# Revit family: Haworth_Planes_ConferenceTable_RectangularTwoPiece
name_source: partatom
category: Furniture Systems
revit_build: Autodesk Revit 2018 (Build: 20170223_1515(x64)
units: mm (PartAtom-declared; Revit-internal decimal feet)

## family parameters
Always vertical = Yes
Cut with Voids When Loaded = No
OmniClass Number = 23.40.70.14.64.21
OmniClass Title = Systems Furniture
Part Type = Normal
Room Calculation Point = No
Round Connector Dimension = Use Diameter
Shared = No
Work Plane-Based = No

## types (36) — shared parameters
Actual Height = 29"
Actual Width = 121"
Assembly Code = E2020200
Base Finish = Haworth _ Laminate _ Maple H-AE
Cable Base = Yes
Center Leg_Interior = No
Center Leg_Perimeter = No
Custom Size = Yes
Description = Haworth - Planes - Conference Table Rectangular - Two-Piece
Half Width = 60 1/2"
Interior Leg = Yes
Manufacturer = Haworth
Max. Depth = 60"
Max. Height = 29"
Max. Width = 180"
Middle Leg_Interior = No
Middle Leg_Perimeter = No
Min. Depth = 42"
Min. Height = 29"
Min. Width = 121"
Min/Max Width = 48-78 @ 6 in. increments
Model = TARA
No Cable Base = No
Perimeter Leg = No
Revision Number = 2
Size = Verify Final Dim. w/ Haworth
Standard Depths = 30, 36, 42, 48, 54, 60 in.
Standard Height = 29 in.
Support Finish = Haworth _ Paint _ Metallic Champagne
Support Height = 27 13/16"
Support Location_Front_Back = 3"
Support Location_Middle = 28 1/4"
Support Location_Side = 3"
Sustainability Info = http://media.haworth.com
Table Thickness = 1 3/16"
URL = www.haworth.com
URL - Product = http://www.haworth.com
Warranty = http://www.haworth.com
Worksurface Edge Finish = Haworth _ Laminate _ Maple H-AE
Worksurface Finish = Haworth _ Laminate _ Maple H-AE

## per-type parameters (varying)
| type | Actual Depth | Depth | Width |
| 48w 30d | 42" | 30" | 48" |
| 54w 30d | 42" | 30" | 54" |
| 60w 30d | 42" | 30" | 60" |
| 66w 30d | 42" | 30" | 66" |
| 72w 30d | 42" | 30" | 72" |
| 78w 30d | 42" | 30" | 78" |
| 48w 36d | 42" | 36" | 48" |
| 54w 36d | 42" | 36" | 54" |
| 60w 36d | 42" | 36" | 60" |
| 66w 36d | 42" | 36" | 66" |
| 72w 36d | 42" | 36" | 72" |
| 78w 36d | 42" | 36" | 78" |
| 48w 42d | 42" | 42" | 48" |
| 54w 42d | 42" | 42" | 54" |
| 60w 42d | 42" | 42" | 60" |
| 66w 42d | 42" | 42" | 66" |
| 72w 42d | 42" | 42" | 72" |
| 78w 42d | 42" | 42" | 78" |
| 48w 48d | 48" | 48" | 48" |
| 54w 48d | 48" | 48" | 54" |
| 60w 48d | 48" | 48" | 60" |
| 66w 48d | 48" | 48" | 66" |
| 72w 48d | 48" | 48" | 72" |
| 78w 48d | 48" | 48" | 78" |
| 48w 54d | 54" | 54" | 48" |
| 54w 54d | 54" | 54" | 54" |
| 60w 54d | 54" | 54" | 60" |
| 66w 54d | 54" | 54" | 66" |
| 72w 54d | 54" | 54" | 72" |
| 78w 54d | 54" | 54" | 78" |
| 48w 60d | 60" | 60" | 48" |
| 54w 60d | 60" | 60" | 54" |
| 60w 60d | 60" | 60" | 60" |
| 66w 60d | 60" | 60" | 66" |
| 72w 60d | 60" | 60" | 72" |
| 78w 60d | 60" | 60" | 78" |

## geometry (parser evidence)
native form markers: Sweep x11
no freeform markers — native parametric forms only
